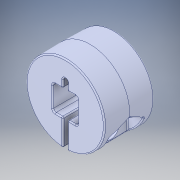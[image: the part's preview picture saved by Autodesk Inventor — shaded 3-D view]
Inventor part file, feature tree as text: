
AUTODESK INVENTOR PART (.ipt)
format: ipt  version: 2017 SP1 (Build 210196100, 196)  size: 396,800 bytes
history: native  units: in
note: dims shown in document units (in); Inventor stores cm internally (conversion verified against a paired STEP export)
features: fillet x1
ambient origin geometry x8: Origin, YZ Plane, XZ Plane, XY Plane, X Axis, Y Axis, Z Axis, Center Point
bodies: Solid1 (feature_tree)
feature tree (1):
  fillet  "Fillet4"  [1 undecoded]
note: 1 required parameter value undecoded (feature->parameter linkage not recoverable at this tier; creation-order binding heuristic only, values carry confidence <= 0.55)
